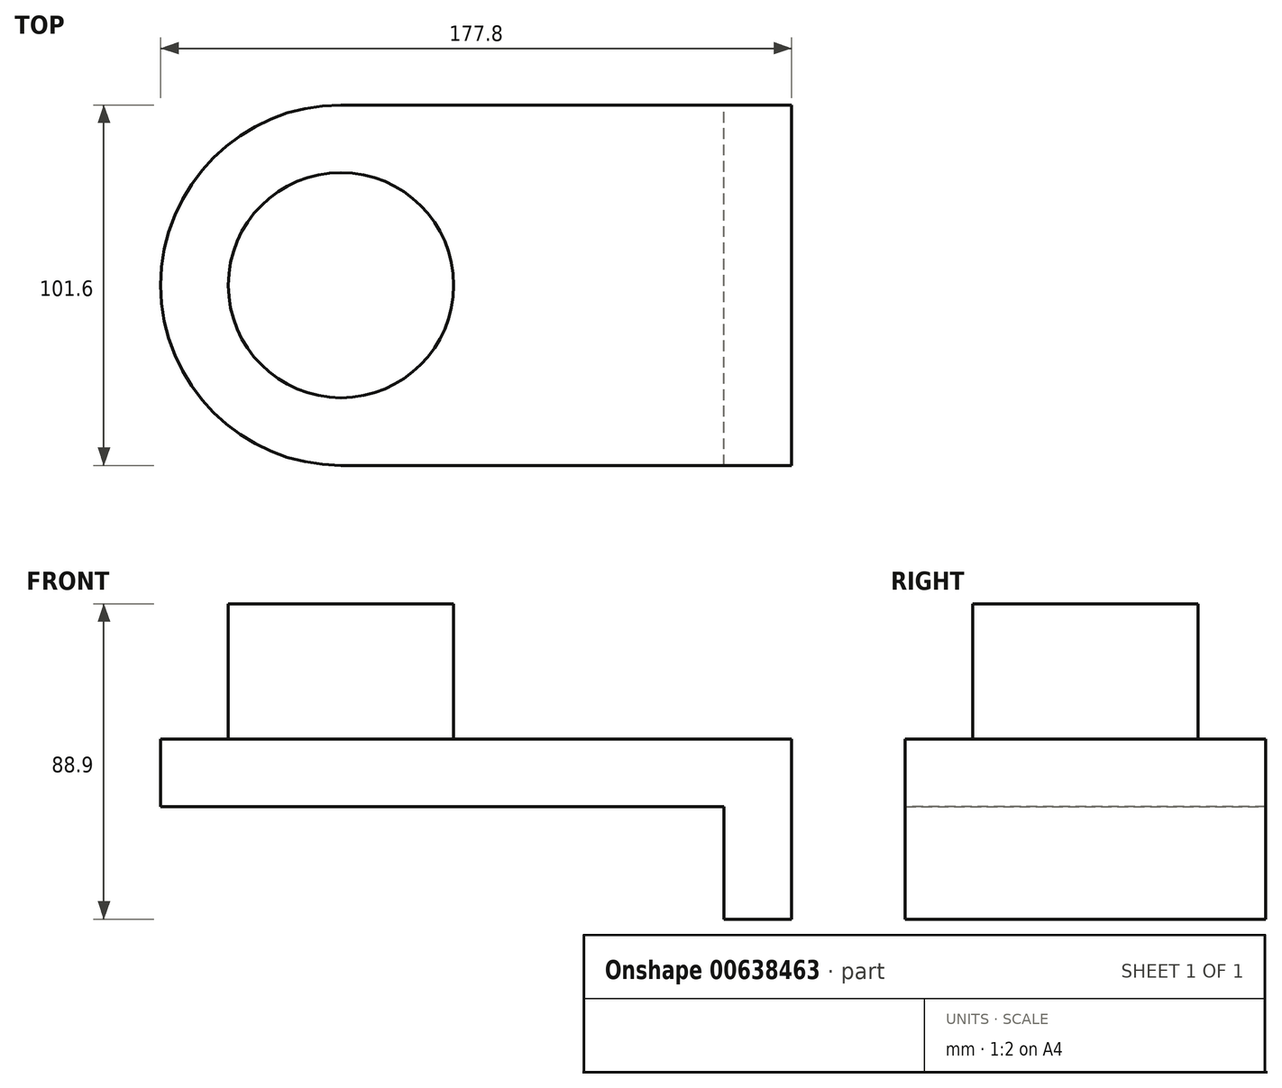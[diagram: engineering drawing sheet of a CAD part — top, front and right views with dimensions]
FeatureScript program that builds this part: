
annotation { "Feature Type Name" : "Feature", "Feature Type Description" : "" }
export const myFeature = defineFeature(function(context is Context, id is Id, definition is map)
    precondition{}
    {
        {
            var Q0;
            Q0=qCreatedBy(makeId("Front.planeOp"),FACE);
            var sketch = newSketch(context, id + "F0", { "sketchPlane" : qUnion([Q0])});
            skLineSegment(sketch, "E0", {"start": v(-74.62, -51.64) * mm, "end": v(84.13, -51.64) * mm});
            skLineSegment(sketch, "E1", {"start": v(-74.62, -51.64) * mm, "end": v(-74.62, -32.59) * mm});
            skLineSegment(sketch, "E2", {"start": v(-74.62, -32.59) * mm, "end": v(103.18, -32.59) * mm});
            skLineSegment(sketch, "E3", {"start": v(84.13, -51.64) * mm, "end": v(84.13, -79.1) * mm});
            skLineSegment(sketch, "E4", {"start": v(103.18, -32.59) * mm, "end": v(103.18, -32.59) * mm});
            skLineSegment(sketch, "E5", {"start": v(103.18, -32.59) * mm, "end": v(103.18, -83.39) * mm});
            skLineSegment(sketch, "E6", {"start": v(103.18, -83.39) * mm, "end": v(84.13, -83.39) * mm});
            skLineSegment(sketch, "E7", {"start": v(84.13, -83.39) * mm, "end": v(84.13, -79.1) * mm});
            skLineSegment(sketch, "E8", {"start": v(84.13, -79.1) * mm, "end": v(84.13, -83.39) * mm});
            skSolve(sketch);
        }
        {
            var Q0;
            Q0 = qSketchRegion(id + "F0", true);
            extrude(context, id + "F1", {"entities" : qUnion([Q0]), "depth" : 101.6 * mm, "offsetDistance" : 25.4 * mm});
        }
        {
            var Q0;
            Q0=makeQuery(id+"F1.opExtrude","CAP_EDGE",EDGE,{"disambiguationData":[OSD([sQuery(id+"F0.wireOp",EDGE,"E1")])],"isStart":true});
            var Q1;
            Q1=makeQuery(id+"F1.opExtrude","CAP_EDGE",EDGE,{"disambiguationData":[OSD([sQuery(id+"F0.wireOp",EDGE,"E1")])],"isStart":false});
            fillet(context, id + "F2", {"entities" : qUnion([Q0, Q1]), "radius" : 50.8 * mm, "tangentPropagation" : true, "allowEdgeOverflow" : false});
        }
        {
            var Q0;
            Q0=makeQuery(id+"F1.opExtrude","SWEPT_FACE",FACE,{"disambiguationData":[OSD([sQuery(id+"F0.wireOp",EDGE,"E2")])]});
            var sketch = newSketch(context, id + "F3", { "sketchPlane" : qUnion([Q0])});
            skCircle(sketch, "E9", {"center": v(-23.82, -50.8) * mm, "radius": 31.75 * mm});
            skSolve(sketch);
        }
        {
            var Q0;
            Q0 = qSketchRegion(id + "F3", true);
            extrude(context, id + "F4", {"entities" : qUnion([Q0]), "operationType" : NewBodyOperationType.ADD, "depth" : 38.1 * mm, "offsetDistance" : 25.4 * mm});
        }
        {
            var Q0;
            Q0=makeQuery(id+"F4.opExtrude","CAP_FACE",FACE,{"disambiguationData":[OSD([sQuery(id+"F3.wireOp",EDGE,"E9")])],"isStart":false});
            var sketch = newSketch(context, id + "F5", { "sketchPlane" : qUnion([Q0])});
            skCircle(sketch, "E10", {"center": v(-23.82, -50.8) * mm, "radius": 12.7 * mm});
            skSolve(sketch);
        }
        {
            var Q0;
            Q0=sQuery(id+"F5.wireOp",EDGE,"E10");
            extrude(context, id + "F6", {"bodyType" : ToolBodyType.SURFACE, "surfaceEntities" : qUnion([Q0]), "depth" : 19.05 * mm, "offsetDistance" : 25.4 * mm});
        }
    });
